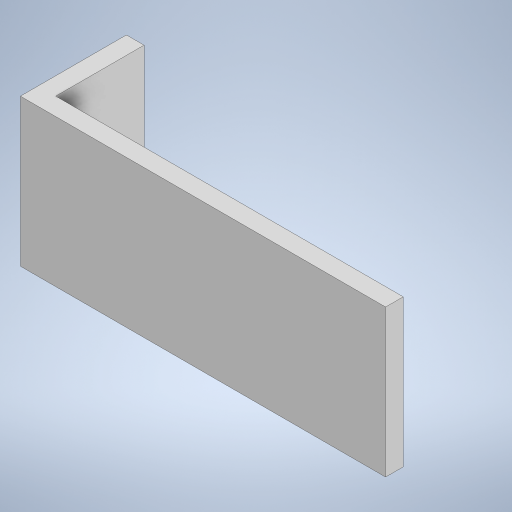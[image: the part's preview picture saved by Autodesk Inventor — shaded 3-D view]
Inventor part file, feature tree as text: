
AUTODESK INVENTOR PART (.ipt)
format: ipt  version: 2023 (Build 270158000, 158)  size: 208,896 bytes
history: native  units: in
note: dims shown in document units (in); Inventor stores cm internally (conversion verified against a paired STEP export)
features: extrude x2, sketch x2
ambient origin geometry x8: Origin, YZ Plane, XZ Plane, XY Plane, X Axis, Y Axis, Z Axis, Center Point
bodies: Solid1 (feature_tree)
feature tree (4):
  extrude  "Extrusion1"  Depth=0.9843in
  extrude  "Extrusion2"  Depth=0.7087in
  sketch  "Sketch1"  dims[d0=2.3228in d1=0.9843in]
  sketch  "Sketch2"  dims[d2=0.1181in d3=0.0in d4=0.7087in d5=0.1181in d6=0.0in]
